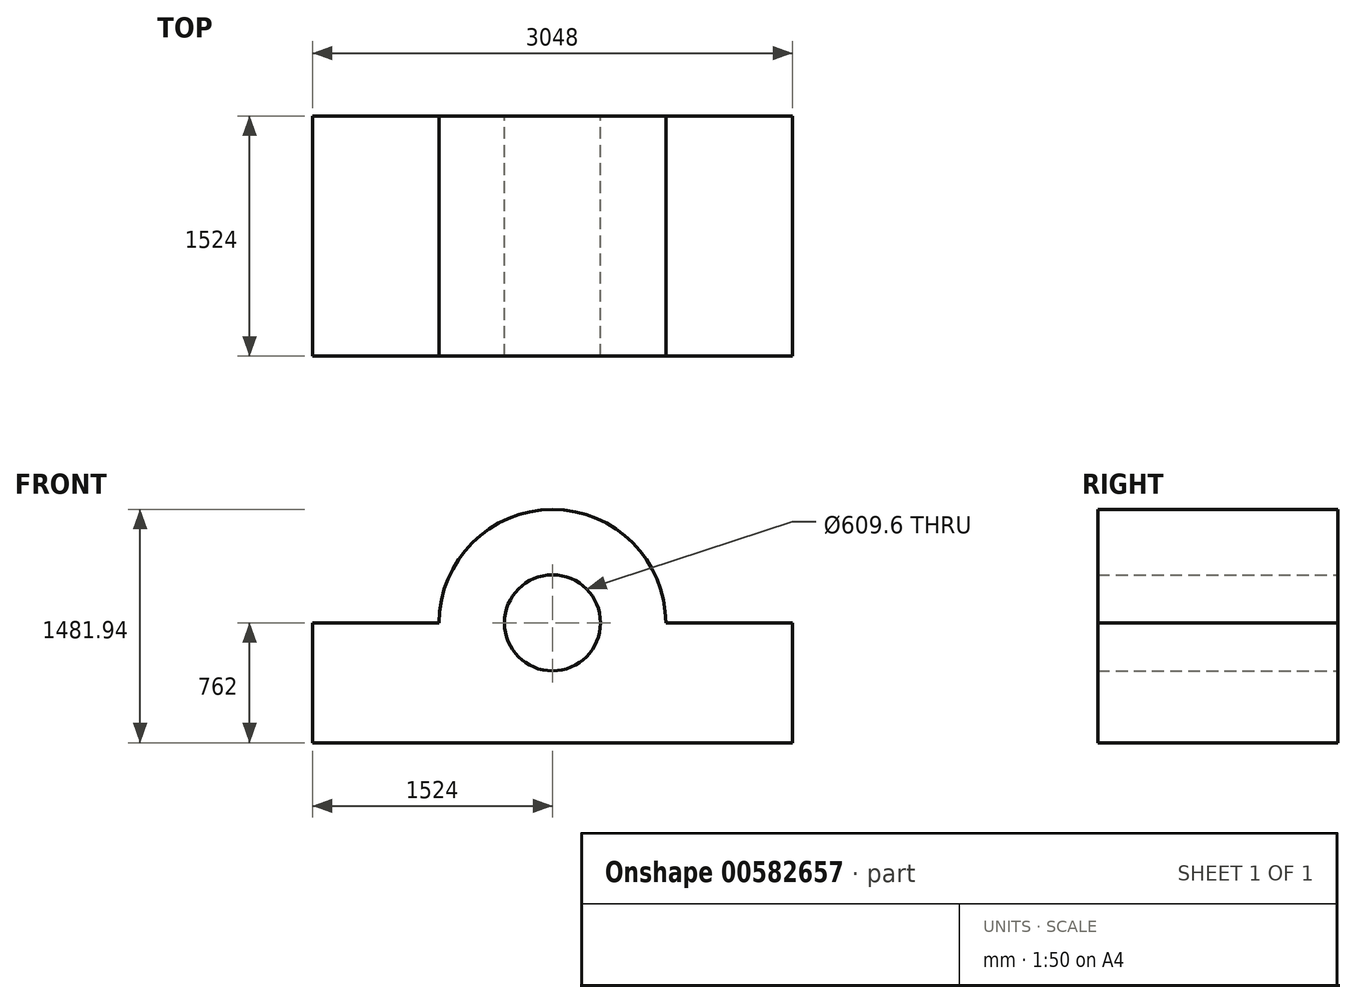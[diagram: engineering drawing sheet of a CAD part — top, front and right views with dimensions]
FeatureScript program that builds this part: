
annotation { "Feature Type Name" : "Feature", "Feature Type Description" : "" }
export const myFeature = defineFeature(function(context is Context, id is Id, definition is map)
    precondition{}
    {
        {
            var Q0;
            Q0=qCreatedBy(makeId("Front.planeOp"),FACE);
            var sketch = newSketch(context, id + "F0", { "sketchPlane" : qUnion([Q0])});
            skLineSegment(sketch, "E0", {"start": v(0, 0) * mm, "end": v(3048, 0) * mm});
            skLineSegment(sketch, "E1", {"start": v(0, 0) * mm, "end": v(0, 762) * mm});
            skArc(sketch, "E2", {"start": v(2243.94, 762) * mm, "mid": v(1524, 1481.94) * mm, "end": v(804.06, 762) * mm});
            skPoint(sketch, "E2.centerSnap0", {"position": v(1524, 0) * mm});
            skLineSegment(sketch, "E3", {"start": v(0, 762) * mm, "end": v(804.06, 762) * mm});
            skLineSegment(sketch, "E4", {"start": v(2243.94, 762) * mm, "end": v(3048, 762) * mm});
            skLineSegment(sketch, "E5", {"start": v(3048, 762) * mm, "end": v(3048, 0) * mm});
            skCircle(sketch, "E6", {"center": v(1524, 762) * mm, "radius": 304.8 * mm});
            skSolve(sketch);
        }
        {
            var Q0;
            Q0 = qSketchRegion(id + "F0", true);
            extrude(context, id + "F1", {"entities" : qUnion([Q0]), "depth" : 1524 * mm, "offsetDistance" : 25.4 * mm});
        }
    });
